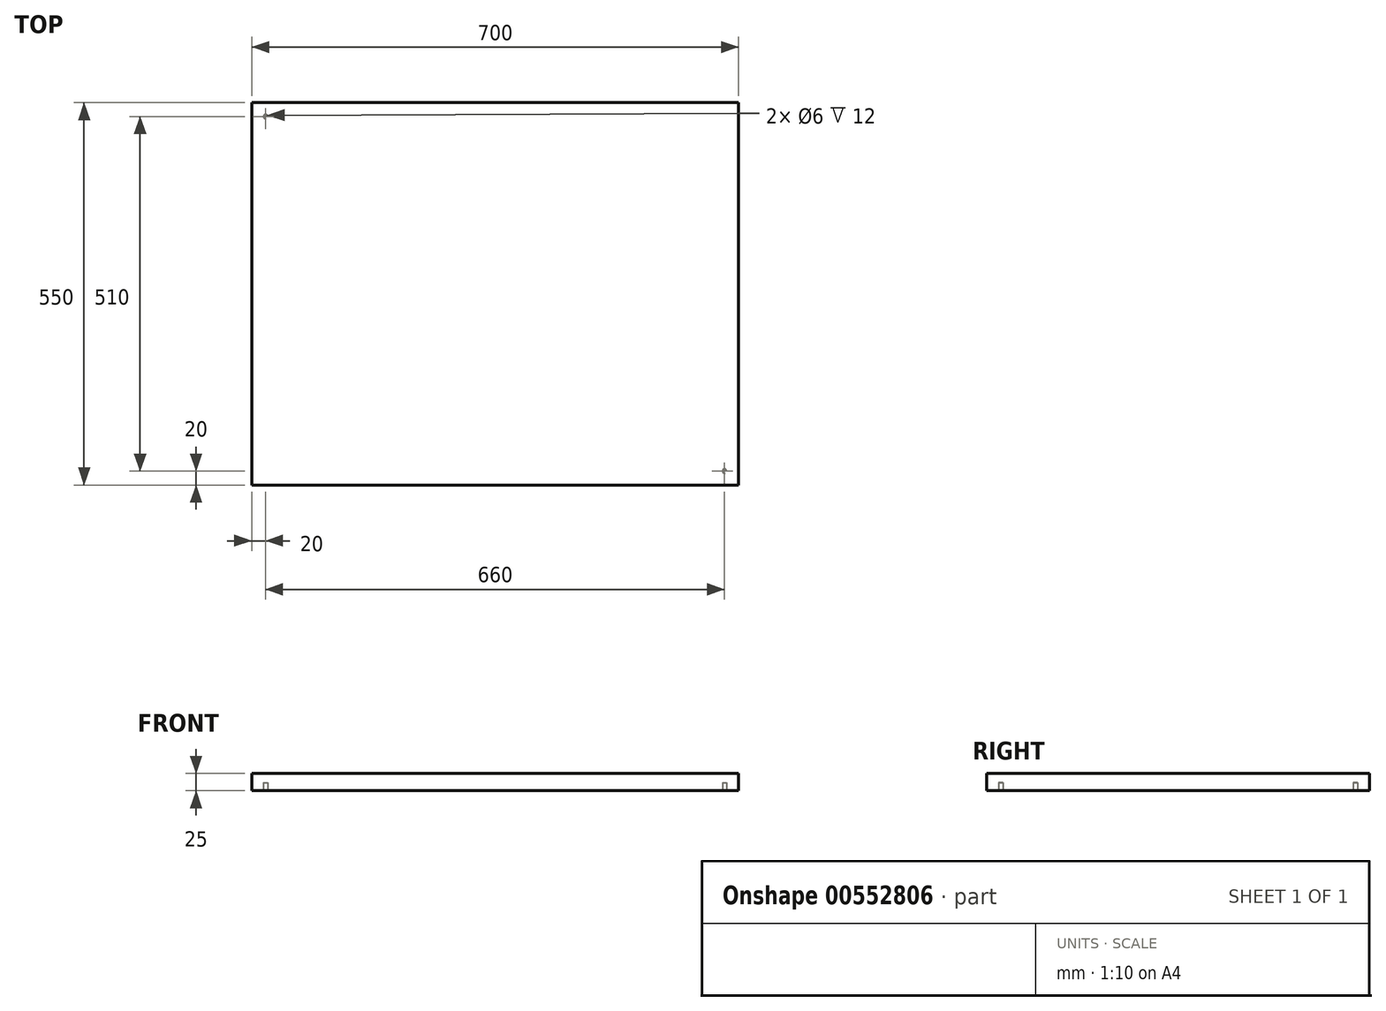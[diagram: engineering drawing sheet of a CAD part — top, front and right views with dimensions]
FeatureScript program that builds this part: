
annotation { "Feature Type Name" : "Feature", "Feature Type Description" : "" }
export const myFeature = defineFeature(function(context is Context, id is Id, definition is map)
    precondition{}
    {
        {
            var Q0;
            Q0=qCreatedBy(makeId("Top.planeOp"),FACE);
            var sketch = newSketch(context, id + "F0", { "sketchPlane" : qUnion([Q0])});
            skLineSegment(sketch, "E0.bottom", {"start": v(350, -275) * mm, "end": v(-350, -275) * mm});
            skLineSegment(sketch, "E0.top", {"start": v(350, 275) * mm, "end": v(-350, 275) * mm});
            skLineSegment(sketch, "E0.left", {"start": v(350, -275) * mm, "end": v(350, 275) * mm});
            skLineSegment(sketch, "E0.right", {"start": v(-350, -275) * mm, "end": v(-350, 275) * mm});
            skPoint(sketch, "E0.middle", {"position": v(0, 0) * mm});
            skSolve(sketch);
        }
        {
            var Q0;
            Q0=makeQuery(id+"F0.imprint","IMPRINT",FACE,{"disambiguationData":[TD([[makeQuery(id+"F0.imprint","IMPRINT",EDGE,{"derivedFrom":sQuery(id+"F0.wireOp",EDGE,"E0.bottom")}),-1.0]])]});
            extrude(context, id + "F1", {"entities" : qUnion([Q0]), "depth" : 25 * mm, "offsetDistance" : 25 * mm});
        }
        {
            var Q0;
            Q0=makeQuery(id+"F1.opExtrude","CAP_FACE",FACE,{"disambiguationData":[OSD([sQuery(id+"F0.wireOp",EDGE,"E0.bottom"),sQuery(id+"F0.wireOp",EDGE,"E0.top"),sQuery(id+"F0.wireOp",EDGE,"E0.left"),sQuery(id+"F0.wireOp",EDGE,"E0.right")])],"isStart":true});
            var sketch = newSketch(context, id + "F2", { "sketchPlane" : qUnion([Q0])});
            skCircle(sketch, "E1", {"center": v(330, 255) * mm, "radius": 3 * mm});
            skSolve(sketch);
        }
        {
            var Q0;
            Q0=makeQuery(id+"F2.imprint","IMPRINT",FACE,{"disambiguationData":[TD([[makeQuery(id+"F2.imprint","IMPRINT",EDGE,{"derivedFrom":sQuery(id+"F2.wireOp",EDGE,"E1")}),1.0]])]});
            extrude(context, id + "F3", {"entities" : qUnion([Q0]), "operationType" : NewBodyOperationType.REMOVE, "oppositeDirection" : true, "depth" : 12 * mm, "offsetDistance" : 25 * mm});
        }
        {
            var Q0;
            Q0=makeQuery(id+"F1.opExtrude","CAP_FACE",FACE,{"disambiguationData":[OSD([sQuery(id+"F0.wireOp",EDGE,"E0.bottom"),sQuery(id+"F0.wireOp",EDGE,"E0.top"),sQuery(id+"F0.wireOp",EDGE,"E0.left"),sQuery(id+"F0.wireOp",EDGE,"E0.right")])],"isStart":true});
            var sketch = newSketch(context, id + "F4", { "sketchPlane" : qUnion([Q0])});
            skCircle(sketch, "E2", {"center": v(-330, -255) * mm, "radius": 3 * mm});
            skSolve(sketch);
        }
        {
            var Q0;
            Q0=makeQuery(id+"F4.imprint","IMPRINT",FACE,{"disambiguationData":[TD([[makeQuery(id+"F4.imprint","IMPRINT",EDGE,{"derivedFrom":sQuery(id+"F4.wireOp",EDGE,"E2")}),1.0]])]});
            extrude(context, id + "F5", {"entities" : qUnion([Q0]), "operationType" : NewBodyOperationType.REMOVE, "oppositeDirection" : true, "depth" : 12 * mm, "offsetDistance" : 25 * mm});
        }
    });
